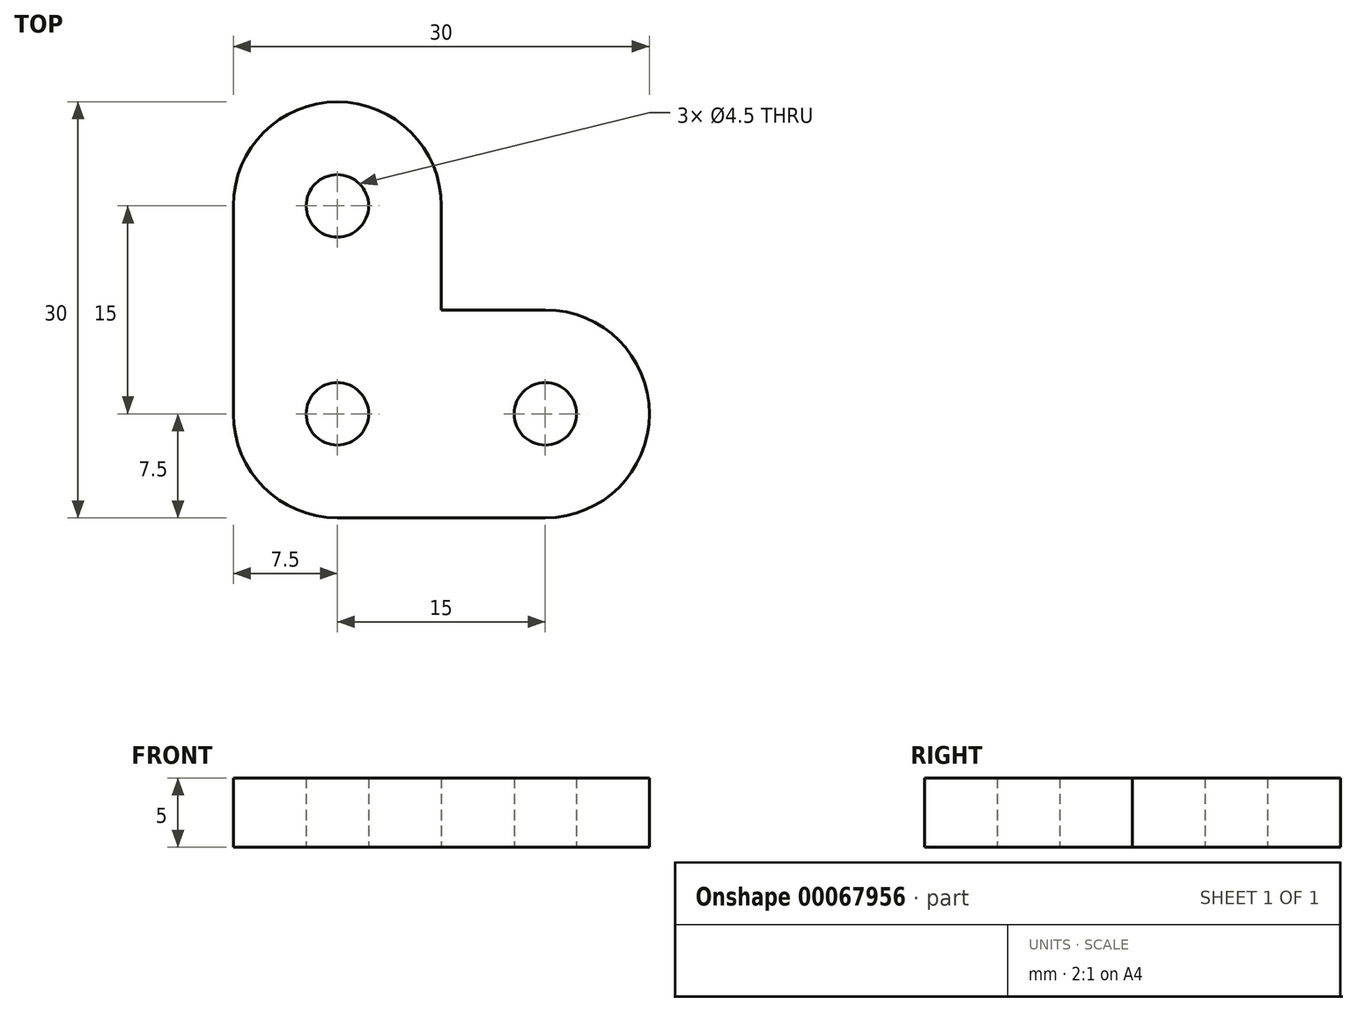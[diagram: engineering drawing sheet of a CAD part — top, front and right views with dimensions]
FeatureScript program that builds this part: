
annotation { "Feature Type Name" : "Feature", "Feature Type Description" : "" }
export const myFeature = defineFeature(function(context is Context, id is Id, definition is map)
    precondition{}
    {
        {
            var Q0;
            Q0=qCreatedBy(makeId("Top.planeOp"),FACE);
            var sketch = newSketch(context, id + "F0", { "sketchPlane" : qUnion([Q0])});
            skLineSegment(sketch, "E0", {"start": v(0, 15) * mm, "end": v(0, 15) * mm});
            skLineSegment(sketch, "E1", {"start": v(-7.5, 7.5) * mm, "end": v(-7.5, -7.5) * mm});
            skLineSegment(sketch, "E2", {"start": v(0, -15) * mm, "end": v(15, -15) * mm});
            skLineSegment(sketch, "E3", {"start": v(22.5, -7.5) * mm, "end": v(22.5, -7.5) * mm});
            skLineSegment(sketch, "E4", {"start": v(15, 0) * mm, "end": v(7.5, 0) * mm});
            skLineSegment(sketch, "E5", {"start": v(7.5, 0) * mm, "end": v(7.5, 7.5) * mm});
            skCircle(sketch, "E6", {"center": v(0, 7.5) * mm, "radius": 2.25 * mm});
            skCircle(sketch, "E7", {"center": v(0, -7.5) * mm, "radius": 2.25 * mm});
            skCircle(sketch, "E8", {"center": v(15, -7.5) * mm, "radius": 2.25 * mm});
            skPoint(sketch, "E9.visualSharp", {"position": v(-7.5, 15) * mm});
            skArc(sketch, "E9.filletArc", {"start": v(0, 15) * mm, "mid": v(-5.3, 12.8) * mm, "end": v(-7.5, 7.5) * mm});
            skPoint(sketch, "E10.visualSharp", {"position": v(7.5, 15) * mm});
            skArc(sketch, "E10.filletArc", {"start": v(7.5, 7.5) * mm, "mid": v(5.3, 12.8) * mm, "end": v(0, 15) * mm});
            skPoint(sketch, "E11.visualSharp", {"position": v(22.5, 0) * mm});
            skArc(sketch, "E11.filletArc", {"start": v(22.5, -7.5) * mm, "mid": v(20.3, -2.2) * mm, "end": v(15, 0) * mm});
            skPoint(sketch, "E12.visualSharp", {"position": v(22.5, -15) * mm});
            skArc(sketch, "E12.filletArc", {"start": v(15, -15) * mm, "mid": v(20.3, -12.8) * mm, "end": v(22.5, -7.5) * mm});
            skPoint(sketch, "E13.visualSharp", {"position": v(-7.5, -15) * mm});
            skArc(sketch, "E13.filletArc", {"start": v(-7.5, -7.5) * mm, "mid": v(-5.3, -12.8) * mm, "end": v(0, -15) * mm});
            skSolve(sketch);
        }
        {
            var Q0;
            Q0 = qSketchRegion(id + "F0", true);
            extrude(context, id + "F1", {"entities" : qUnion([Q0]), "depth" : 5 * mm});
        }
    });
